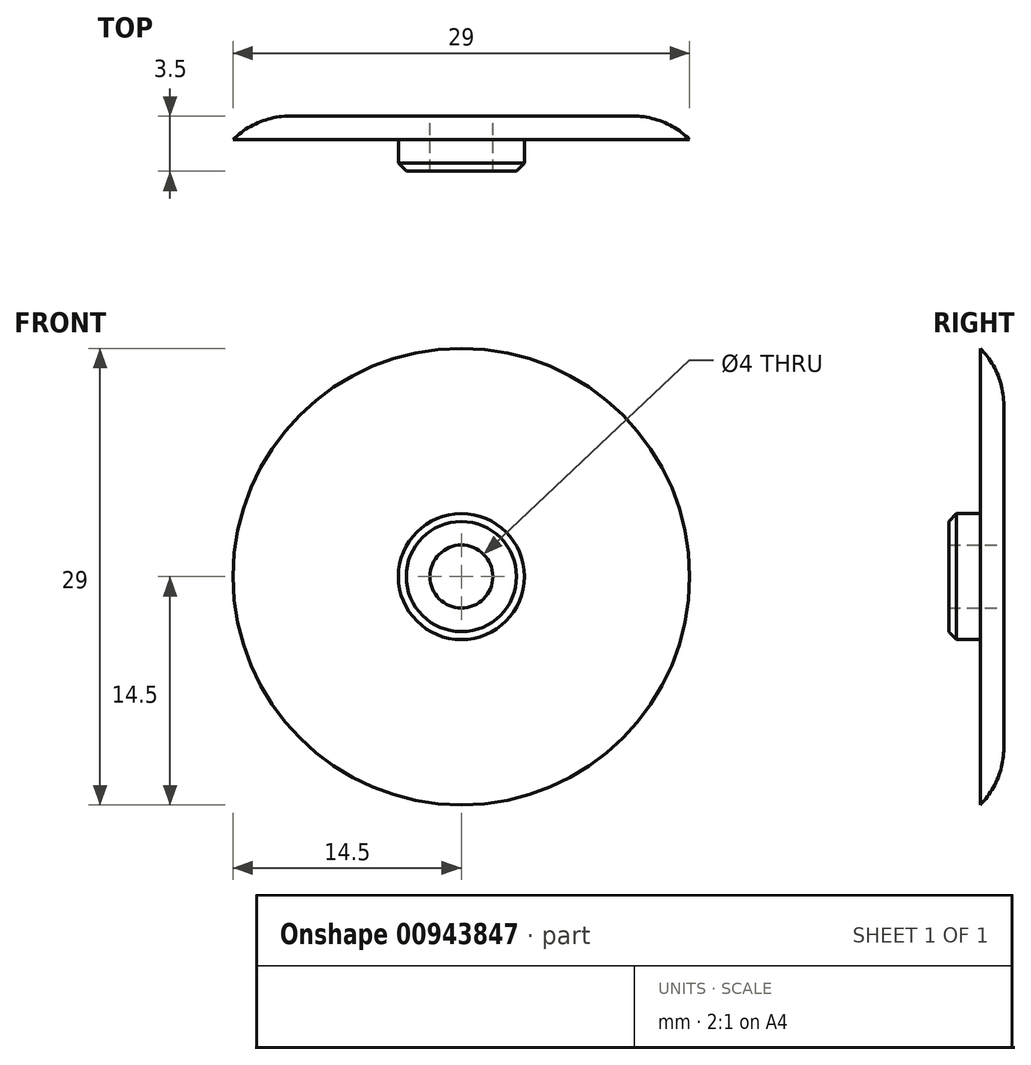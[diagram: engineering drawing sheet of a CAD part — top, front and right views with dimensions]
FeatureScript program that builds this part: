
annotation { "Feature Type Name" : "Feature", "Feature Type Description" : "" }
export const myFeature = defineFeature(function(context is Context, id is Id, definition is map)
    precondition{}
    {
        {
            var Q0;
            Q0=qCreatedBy(makeId("Front.planeOp"),FACE);
            var sketch = newSketch(context, id + "F0", { "sketchPlane" : qUnion([Q0])});
            skCircle(sketch, "E0", {"center": v(0, 0) * mm, "radius": 14.5 * mm});
            skCircle(sketch, "E1", {"center": v(0, 0) * mm, "radius": 4 * mm});
            skCircle(sketch, "E2", {"center": v(0, 0) * mm, "radius": 2 * mm});
            skSolve(sketch);
        }
        {
            var Q0;
            Q0=makeQuery(id+"F0.imprint","IMPRINT",FACE,{"disambiguationData":[TD([[makeQuery(id+"F0.imprint","IMPRINT",EDGE,{"derivedFrom":sQuery(id+"F0.wireOp",EDGE,"E0")}),1.0]])]});
            extrude(context, id + "F1", {"entities" : qUnion([Q0]), "depth" : 1.5 * mm, "offsetDistance" : 25.4 * mm});
        }
        {
            var Q0;
            Q0=makeQuery(id+"F0.imprint","IMPRINT",FACE,{"disambiguationData":[TD([[makeQuery(id+"F0.imprint","IMPRINT",EDGE,{"derivedFrom":sQuery(id+"F0.wireOp",EDGE,"E1")}),1.0]])]});
            extrude(context, id + "F2", {"entities" : qUnion([Q0]), "operationType" : NewBodyOperationType.ADD, "depth" : 3.5 * mm, "offsetDistance" : 25.4 * mm});
        }
        {
            var Q0;
            Q0=makeQuery(id+"F2.opExtrude","CAP_EDGE",EDGE,{"disambiguationData":[OSD([sQuery(id+"F0.wireOp",EDGE,"E1")])],"isStart":false});
            chamfer(context, id + "F3", {"entities" : qUnion([Q0]), "width" : .5 * mm, "tangentPropagation" : true});
        }
        {
            var Q0;
            Q0=makeQuery(id+"F1.opExtrude","CAP_EDGE",EDGE,{"disambiguationData":[OSD([sQuery(id+"F0.wireOp",EDGE,"E0")])],"isStart":true});
            fillet(context, id + "F4", {"entities" : qUnion([Q0]), "radius" : 5.08 * mm, "tangentPropagation" : true, "allowEdgeOverflow" : false});
        }
    });
